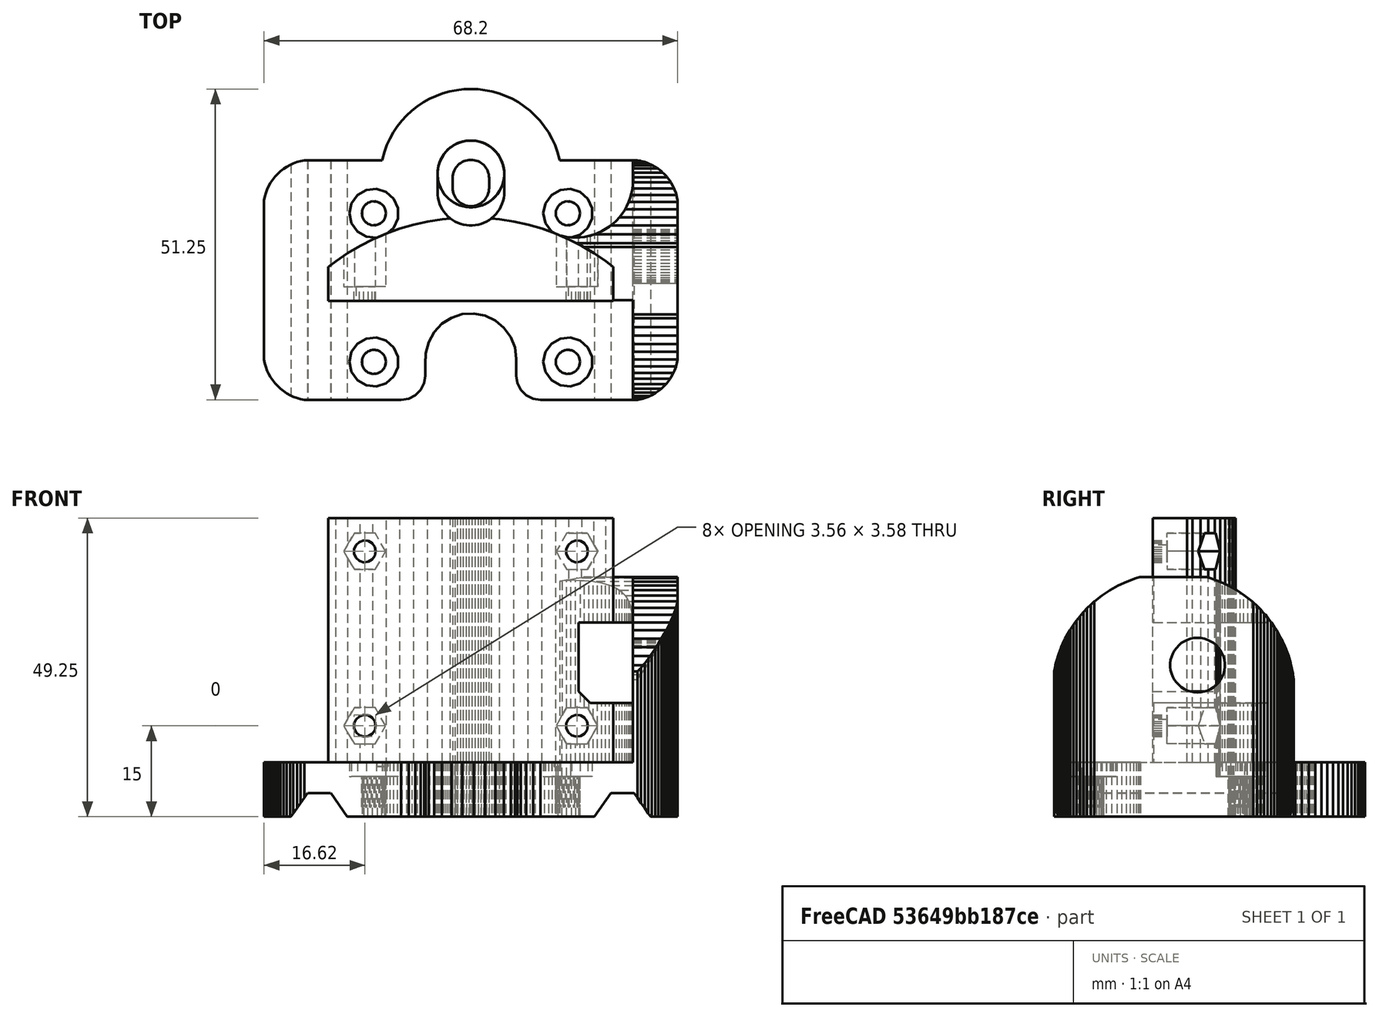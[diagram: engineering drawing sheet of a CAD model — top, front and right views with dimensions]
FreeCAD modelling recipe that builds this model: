
FCSTD DOCUMENT  (FreeCAD 0.15R4619 (Git))
Label: x_end_idler_M5
License: All rights reserved
LicenseURL: http://en.wikipedia.org/wiki/All_rights_reserved
objects: Part::Feature×1, Sketcher::SketchObject×1, PartDesign::Pad×1
note: 4 computed .brp shape members not serialized (recipe doc carries the construction recipe); baked Part::Feature solids carry a one-line shape summary decoded from their .brp

FEATURE [Part::Feature] Solid
  shape: bbox 68.2 x 51.25 x 49.25 mm, 1250 faces (baked)
FEATURE [Sketcher::SketchObject] Sketch
  ExternalGeometry = -> [Solid]
  Placement = pos=(0,0,4.5) rot=(0,0,1;0rad)
  Support = -> Solid [Face545]
  sketch-geometry (15):
    g0: LineSegment [constr] StartX=-5.5 StartY=14.5 StartZ=0 EndX=5.5 EndY=11.5 EndZ=0
    g1: LineSegment [constr] StartX=5.5 StartY=14.5 StartZ=0 EndX=-5.5 EndY=11.5 EndZ=0
    g2: GeomPoint [constr] X=0 Y=13 Z=0
    g3: LineSegment [constr] StartX=0 StartY=12.1818 StartZ=0 EndX=0 EndY=13 EndZ=0
    g4: LineSegment [constr] StartX=0 StartY=13 StartZ=0 EndX=0 EndY=13.8182 EndZ=0
    g5: ArcOfCircle CenterX=0 CenterY=13.8182 CenterZ=0 NormalX=0 NormalY=0 NormalZ=1 Radius=3 StartAngle=0 EndAngle=3.14159
    g6: ArcOfCircle CenterX=0 CenterY=12.1818 CenterZ=0 NormalX=0 NormalY=0 NormalZ=1 Radius=3 StartAngle=3.14159 EndAngle=6.28319
    g7: LineSegment StartX=-3 StartY=12.1818 StartZ=0 EndX=-3 EndY=13.8182 EndZ=0
    g8: LineSegment StartX=3 StartY=13.8182 StartZ=0 EndX=3 EndY=12.1818 EndZ=0
    g9: LineSegment [constr] StartX=-3 StartY=13.8182 StartZ=0 EndX=3 EndY=13.8182 EndZ=0
    g10: LineSegment [constr] StartX=3 StartY=12.1818 StartZ=0 EndX=-3 EndY=12.1818 EndZ=0
    g11: ArcOfCircle CenterX=0 CenterY=14.5 CenterZ=0 NormalX=0 NormalY=0 NormalZ=1 Radius=5.5 StartAngle=6.28318 EndAngle=9.42478
    g12: ArcOfCircle CenterX=0 CenterY=11.5 CenterZ=0 NormalX=0 NormalY=0 NormalZ=1 Radius=5.5 StartAngle=3.14159 EndAngle=6.28318
    g13: LineSegment StartX=-5.5 StartY=11.5 StartZ=0 EndX=-5.5 EndY=14.5 EndZ=0
    g14: LineSegment StartX=5.5 StartY=14.5 StartZ=0 EndX=5.5 EndY=11.5 EndZ=0
  constraints (38):
    c: Coincident(g0,g-3)
    c: Coincident(g0,g-6)
    c: Coincident(g1,g-4)
    c: Coincident(g1,g-5)
    c: PointOnObject(g2,g1)
    c: PointOnObject(g2,g0)
    c: Coincident(g3,g2)
    c: Vertical(g3)
    c: Coincident(g3,g4)
    c: Vertical(g4)
    c: Equal(g4,g3)
    c: Coincident(g5,g4)
    c: Coincident(g6,g3)
    c: Coincident(g7,g6)
    c: Coincident(g7,g5)
    c: Vertical(g7)
    c: Coincident(g8,g5)
    c: Coincident(g8,g6)
    c: Coincident(g9,g5)
    c: Coincident(g9,g5)
    c: PointOnObject(g4,g9)
    c: Horizontal(g9)
    c: Coincident(g10,g6)
    c: Coincident(g10,g6)
    c: PointOnObject(g3,g10)
    c: Horizontal(g10)
    c: Radius(g5) = 3
    c: Coincident(g11,g0)
    c: Coincident(g11,g1)
    c: PointOnObject(g-7,g11)
    c: Coincident(g12,g0)
    c: Coincident(g12,g1)
    c: PointOnObject(g-8,g12)
    c: Coincident(g13,g1)
    c: Coincident(g13,g0)
    c: Coincident(g14,g1)
    c: Coincident(g14,g0)
    c: PointOnObject(g5,g1)
FEATURE [PartDesign::Pad] Pad
  Length = 9
  Length2 = 100
  Reversed = true
  Sketch = -> Sketch
  Type = 0
